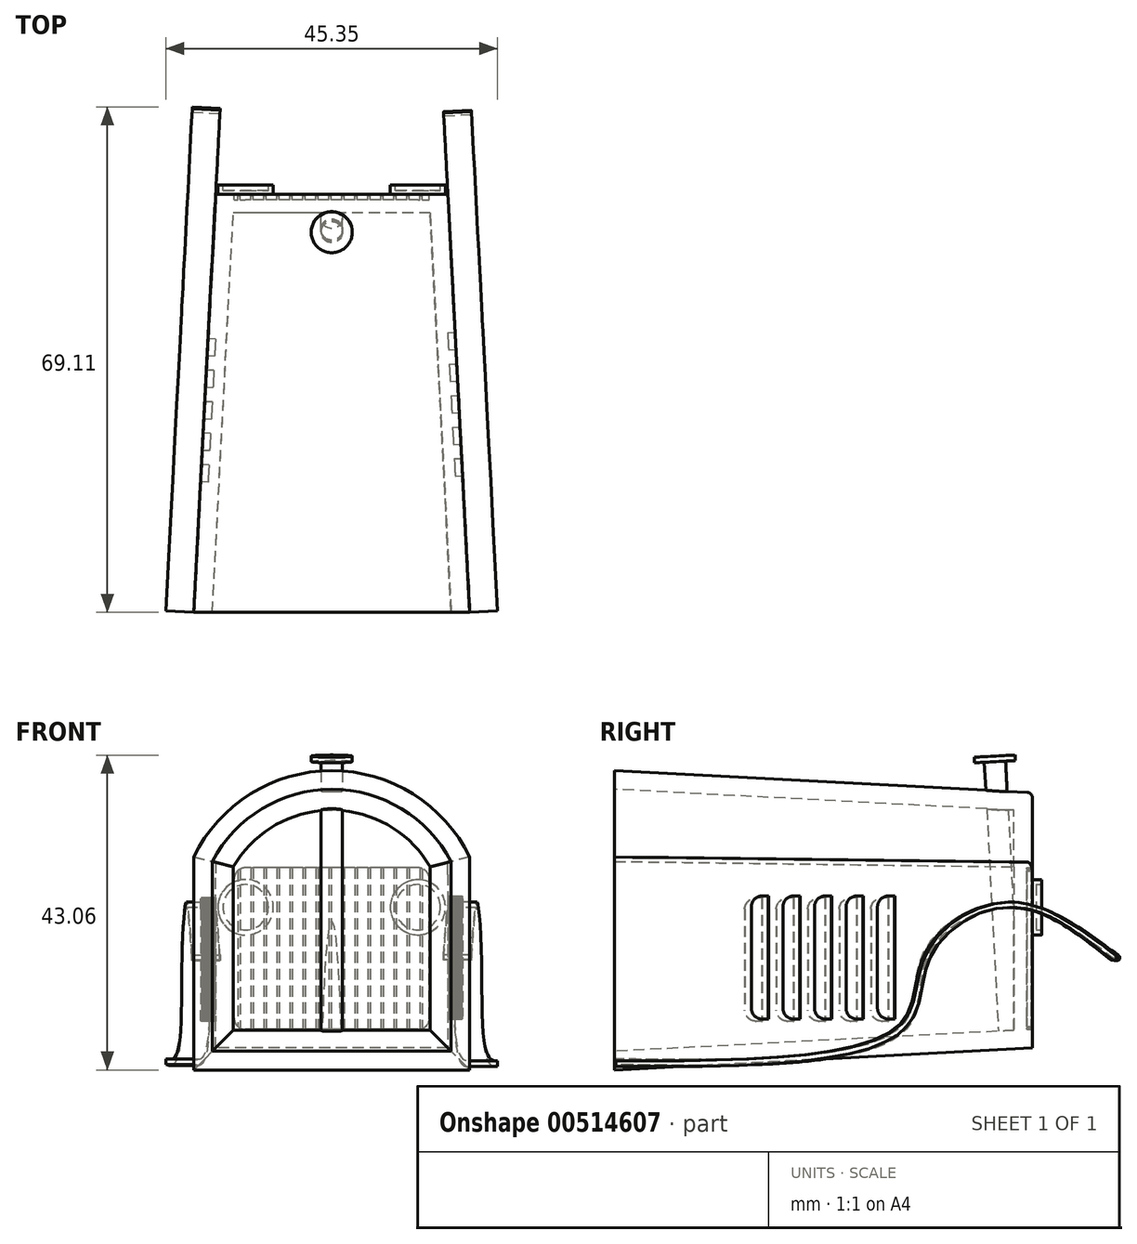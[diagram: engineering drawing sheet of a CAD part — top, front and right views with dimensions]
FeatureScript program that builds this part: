
annotation { "Feature Type Name" : "Feature", "Feature Type Description" : "" }
export const myFeature = defineFeature(function(context is Context, id is Id, definition is map)
    precondition{}
    {
        {
            var Q0;
            Q0=qCreatedBy(makeId("Front.planeOp"),FACE);
            var sketch = newSketch(context, id + "F0", { "sketchPlane" : qUnion([Q0])});
            skLineSegment(sketch, "E0.bottom", {"start": v(15.88, -12.7) * mm, "end": v(-15.88, -12.7) * mm});
            skLineSegment(sketch, "E0.top", {"start": v(15.88, 12.7) * mm, "end": v(-15.88, 12.7) * mm});
            skLineSegment(sketch, "E0.left", {"start": v(15.88, -12.7) * mm, "end": v(15.88, 12.7) * mm});
            skLineSegment(sketch, "E0.right", {"start": v(-15.88, -12.7) * mm, "end": v(-15.88, 12.7) * mm});
            skPoint(sketch, "E0.middle", {"position": v(0, 0) * mm});
            skArc(sketch, "E1", {"start": v(15.88, 12.7) * mm, "mid": v(0, 22.23) * mm, "end": v(-15.88, 12.7) * mm});
            skSolve(sketch);
        }
        {
            var Q0;
            Q0=makeQuery(id+"F0.imprint","IMPRINT",FACE,{"disambiguationData":[TD([[makeQuery(id+"F0.imprint","IMPRINT",EDGE,{"derivedFrom":sQuery(id+"F0.wireOp",EDGE,"E0.bottom")}),-1.0]])]});
            var Q1;
            Q1=makeQuery(id+"F0.imprint","IMPRINT",FACE,{"disambiguationData":[TD([[makeQuery(id+"F0.imprint","IMPRINT",EDGE,{"derivedFrom":sQuery(id+"F0.wireOp",EDGE,"E0.top")}),-1.0]])]});
            extrude(context, id + "F1", {"entities" : qUnion([Q0, Q1]), "depth" : 57.15 * mm, "offsetDistance" : 25.4 * mm, "hasDraft" : true, "draftAngle" : 3 * degree});
        }
        {
            var Q0;
            Q0=makeQuery(id+"F1.opExtrude","CAP_FACE",FACE,{"disambiguationData":[OSD([sQuery(id+"F0.wireOp",EDGE,"E0.bottom"),sQuery(id+"F0.wireOp",EDGE,"E0.left"),sQuery(id+"F0.wireOp",EDGE,"E0.right"),sQuery(id+"F0.wireOp",EDGE,"E1")])],"isStart":false});
            shell(context, id + "F2", {"entities" : qUnion([Q0]), "thickness" : 2.54 * mm});
        }
        {
            var Q0;
            Q0=makeQuery(id+"F1.opExtrude","CAP_FACE",FACE,{"disambiguationData":[OSD([sQuery(id+"F0.wireOp",EDGE,"E0.bottom"),sQuery(id+"F0.wireOp",EDGE,"E0.left"),sQuery(id+"F0.wireOp",EDGE,"E0.right"),sQuery(id+"F0.wireOp",EDGE,"E1")])],"isStart":true});
            var sketch = newSketch(context, id + "F3", { "sketchPlane" : qUnion([Q0])});
            skLineSegment(sketch, "E2.0", {"start": v(-13.33, -8.64) * mm, "end": v(-13.34, 10.41) * mm});
            skLineSegment(sketch, "E2.1", {"start": v(-11.81, -10.16) * mm, "end": v(11.81, -10.16) * mm});
            skLineSegment(sketch, "E2.2", {"start": v(13.33, -8.64) * mm, "end": v(13.33, 10.41) * mm});
            skLineSegment(sketch, "E3", {"start": v(-11.81, 11.94) * mm, "end": v(11.81, 11.94) * mm});
            skPoint(sketch, "E4.visualSharp", {"position": v(-13.33, 11.94) * mm});
            skArc(sketch, "E4.filletArc", {"start": v(-11.81, 11.94) * mm, "mid": v(-12.89, 11.5) * mm, "end": v(-13.33, 10.41) * mm});
            skPoint(sketch, "E5.visualSharp", {"position": v(13.33, 11.94) * mm});
            skArc(sketch, "E5.filletArc", {"start": v(13.33, 10.41) * mm, "mid": v(12.89, 11.5) * mm, "end": v(11.81, 11.94) * mm});
            skPoint(sketch, "E6.visualSharp", {"position": v(13.33, -10.16) * mm});
            skArc(sketch, "E6.filletArc", {"start": v(11.81, -10.16) * mm, "mid": v(12.89, -9.71) * mm, "end": v(13.33, -8.64) * mm});
            skPoint(sketch, "E7.visualSharp", {"position": v(-13.33, -10.16) * mm});
            skArc(sketch, "E7.filletArc", {"start": v(-13.33, -8.64) * mm, "mid": v(-12.89, -9.71) * mm, "end": v(-11.81, -10.16) * mm});
            skSolve(sketch);
        }
        {
            var Q0;
            Q0 = qSketchRegion(id + "F3", true);
            extrude(context, id + "F4", {"entities" : qUnion([Q0]), "operationType" : NewBodyOperationType.REMOVE, "oppositeDirection" : true, "depth" : 0.76 * mm, "offsetDistance" : 25.4 * mm});
        }
        {
            var Q0;
            Q0=makeQuery(id+"F1.opExtrude","SWEPT_FACE",FACE,{"disambiguationData":[OSD([sQuery(id+"F0.wireOp",EDGE,"E0.right")])]});
            var sketch = newSketch(context, id + "F5", { "sketchPlane" : qUnion([Q0])});
            skLineSegment(sketch, "E8.bottom", {"start": v(20.57, 7.81) * mm, "end": v(21.4, 7.81) * mm});
            skLineSegment(sketch, "E8.top", {"start": v(20.57, -9.03) * mm, "end": v(21.4, -9.03) * mm});
            skLineSegment(sketch, "E8.left", {"start": v(20.57, 7.81) * mm, "end": v(20.57, -9.03) * mm});
            skLineSegment(sketch, "E8.right", {"start": v(22.93, 6.3) * mm, "end": v(22.93, -7.5) * mm});
            skPoint(sketch, "E9.visualSharp", {"position": v(22.93, 7.81) * mm});
            skArc(sketch, "E9.filletArc", {"start": v(22.93, 6.3) * mm, "mid": v(22.49, 7.37) * mm, "end": v(21.4, 7.81) * mm});
            skPoint(sketch, "E10.visualSharp", {"position": v(22.93, -9.03) * mm});
            skArc(sketch, "E10.filletArc", {"start": v(21.4, -9.03) * mm, "mid": v(22.49, -8.59) * mm, "end": v(22.93, -7.5) * mm});
            skLineSegment(sketch, "E11.1.0.0", {"start": v(24.9, 7.81) * mm, "end": v(24.9, -9.03) * mm});
            skLineSegment(sketch, "E11.1.0.1", {"start": v(27.25, 6.3) * mm, "end": v(27.25, -7.5) * mm});
            skLineSegment(sketch, "E11.1.0.2", {"start": v(24.9, 7.81) * mm, "end": v(25.73, 7.81) * mm});
            skArc(sketch, "E11.1.0.3", {"start": v(27.25, 6.3) * mm, "mid": v(26.8, 7.37) * mm, "end": v(25.73, 7.81) * mm});
            skLineSegment(sketch, "E11.1.0.4", {"start": v(24.9, -9.03) * mm, "end": v(25.73, -9.03) * mm});
            skArc(sketch, "E11.1.0.5", {"start": v(25.73, -9.03) * mm, "mid": v(26.8, -8.59) * mm, "end": v(27.25, -7.5) * mm});
            skLineSegment(sketch, "E11.2.0.0", {"start": v(29.2, 7.81) * mm, "end": v(29.2, -9.03) * mm});
            skLineSegment(sketch, "E11.2.0.1", {"start": v(31.57, 6.3) * mm, "end": v(31.57, -7.5) * mm});
            skLineSegment(sketch, "E11.2.0.2", {"start": v(29.2, 7.81) * mm, "end": v(30.05, 7.81) * mm});
            skArc(sketch, "E11.2.0.3", {"start": v(31.57, 6.3) * mm, "mid": v(31.12, 7.37) * mm, "end": v(30.05, 7.81) * mm});
            skLineSegment(sketch, "E11.2.0.4", {"start": v(29.2, -9.03) * mm, "end": v(30.05, -9.03) * mm});
            skArc(sketch, "E11.2.0.5", {"start": v(30.05, -9.03) * mm, "mid": v(31.12, -8.59) * mm, "end": v(31.57, -7.5) * mm});
            skLineSegment(sketch, "E11.3.0.0", {"start": v(33.53, 7.81) * mm, "end": v(33.53, -9.03) * mm});
            skLineSegment(sketch, "E11.3.0.1", {"start": v(35.89, 6.3) * mm, "end": v(35.89, -7.5) * mm});
            skLineSegment(sketch, "E11.3.0.2", {"start": v(33.53, 7.81) * mm, "end": v(34.36, 7.81) * mm});
            skArc(sketch, "E11.3.0.3", {"start": v(35.89, 6.3) * mm, "mid": v(35.44, 7.37) * mm, "end": v(34.36, 7.81) * mm});
            skLineSegment(sketch, "E11.3.0.4", {"start": v(33.53, -9.03) * mm, "end": v(34.36, -9.03) * mm});
            skArc(sketch, "E11.3.0.5", {"start": v(34.36, -9.03) * mm, "mid": v(35.44, -8.59) * mm, "end": v(35.89, -7.5) * mm});
            skLineSegment(sketch, "E11.4.0.0", {"start": v(37.85, 7.81) * mm, "end": v(37.85, -9.03) * mm});
            skLineSegment(sketch, "E11.4.0.1", {"start": v(40.2, 6.3) * mm, "end": v(40.2, -7.5) * mm});
            skLineSegment(sketch, "E11.4.0.2", {"start": v(37.85, 7.81) * mm, "end": v(38.68, 7.81) * mm});
            skArc(sketch, "E11.4.0.3", {"start": v(40.2, 6.3) * mm, "mid": v(39.76, 7.37) * mm, "end": v(38.68, 7.81) * mm});
            skLineSegment(sketch, "E11.4.0.4", {"start": v(37.85, -9.03) * mm, "end": v(38.68, -9.03) * mm});
            skArc(sketch, "E11.4.0.5", {"start": v(38.68, -9.03) * mm, "mid": v(39.76, -8.59) * mm, "end": v(40.2, -7.5) * mm});
            skLineSegment(sketch, "E11.direction1", {"start": v(20.57, -9.03) * mm, "end": v(24.9, -9.03) * mm, "construction": true});
            skSolve(sketch);
        }
        {
            var Q0;
            Q0 = qSketchRegion(id + "F5", true);
            extrude(context, id + "F6", {"entities" : qUnion([Q0]), "operationType" : NewBodyOperationType.REMOVE, "oppositeDirection" : true, "depth" : 1.02 * mm, "offsetDistance" : 25.4 * mm});
        }
        {
            var Q0;
            Q0=makeQuery(id+"F1.opExtrude","CAP_EDGE",EDGE,{"disambiguationData":[OSD([sQuery(id+"F0.wireOp",EDGE,"E1")])],"isStart":true});
            fillet(context, id + "F7", {"entities" : qUnion([Q0]), "radius" : 0.76 * mm, "tangentPropagation" : true, "allowEdgeOverflow" : false});
        }
        {
            var Q0;
            Q0=makeQuery(id+"F1.opExtrude","SWEPT_FACE",FACE,{"disambiguationData":[OSD([sQuery(id+"F0.wireOp",EDGE,"E0.left")])]});
            var sketch = newSketch(context, id + "F8", { "sketchPlane" : qUnion([Q0])});
            skPoint(sketch, "E12.visualSharp", {"position": v(-36.83, 8.1) * mm});
            skPoint(sketch, "E13.visualSharp", {"position": v(-36.83, -8.75) * mm});
            skLineSegment(sketch, "E14.MirrorCS", {"start": v(-24.02, -8.75) * mm, "end": v(-24.86, -8.75) * mm});
            skLineSegment(sketch, "E15.MirrorCS", {"start": v(-28.34, 8.1) * mm, "end": v(-29.17, 8.1) * mm});
            skLineSegment(sketch, "E16.MirrorCS", {"start": v(-19.7, -8.75) * mm, "end": v(-20.54, -8.75) * mm});
            skLineSegment(sketch, "E17.MirrorCS", {"start": v(-24.02, 8.1) * mm, "end": v(-24.86, 8.1) * mm});
            skLineSegment(sketch, "E18.MirrorCS", {"start": v(-32.65, -8.75) * mm, "end": v(-33.5, -8.75) * mm});
            skLineSegment(sketch, "E19.MirrorCS", {"start": v(-19.7, 8.1) * mm, "end": v(-20.54, 8.1) * mm});
            skLineSegment(sketch, "E20.MirrorCS", {"start": v(-36.97, 8.1) * mm, "end": v(-37.8, 8.1) * mm});
            skLineSegment(sketch, "E21.MirrorCS", {"start": v(-28.34, -8.75) * mm, "end": v(-29.17, -8.75) * mm});
            skLineSegment(sketch, "E22.MirrorCS", {"start": v(-32.65, 8.1) * mm, "end": v(-33.5, 8.1) * mm});
            skLineSegment(sketch, "E23.MirrorCS", {"start": v(-36.97, -8.75) * mm, "end": v(-37.8, -8.75) * mm});
            skArc(sketch, "E24.MirrorCS", {"start": v(-22.06, 6.57) * mm, "mid": v(-21.61, 7.65) * mm, "end": v(-20.54, 8.1) * mm});
            skArc(sketch, "E25.MirrorCS", {"start": v(-20.54, -8.75) * mm, "mid": v(-21.61, -8.3) * mm, "end": v(-22.06, -7.23) * mm});
            skArc(sketch, "E26.MirrorCS", {"start": v(-30.7, 6.57) * mm, "mid": v(-30.25, 7.65) * mm, "end": v(-29.17, 8.1) * mm});
            skLineSegment(sketch, "E27.MirrorCS", {"start": v(-19.7, 8.1) * mm, "end": v(-19.7, -8.75) * mm});
            skLineSegment(sketch, "E28.MirrorCS", {"start": v(-36.97, 8.1) * mm, "end": v(-36.97, -8.75) * mm});
            skLineSegment(sketch, "E29.MirrorCS", {"start": v(-22.06, 6.57) * mm, "end": v(-22.06, -7.23) * mm});
            skArc(sketch, "E30.MirrorCS", {"start": v(-24.86, -8.75) * mm, "mid": v(-25.93, -8.3) * mm, "end": v(-26.38, -7.23) * mm});
            skLineSegment(sketch, "E31.MirrorCS", {"start": v(-32.65, 8.1) * mm, "end": v(-32.65, -8.75) * mm});
            skLineSegment(sketch, "E32.MirrorCS", {"start": v(-30.7, 6.57) * mm, "end": v(-30.7, -7.23) * mm});
            skLineSegment(sketch, "E33.MirrorCS", {"start": v(-39.33, 6.57) * mm, "end": v(-39.33, -7.23) * mm});
            skLineSegment(sketch, "E34.MirrorCS", {"start": v(-24.02, 8.1) * mm, "end": v(-24.02, -8.75) * mm});
            skLineSegment(sketch, "E35.MirrorCS", {"start": v(-26.38, 6.57) * mm, "end": v(-26.38, -7.23) * mm});
            skArc(sketch, "E36.MirrorCS", {"start": v(-26.38, 6.57) * mm, "mid": v(-25.93, 7.65) * mm, "end": v(-24.86, 8.1) * mm});
            skLineSegment(sketch, "E37.MirrorCS", {"start": v(-28.34, 8.1) * mm, "end": v(-28.34, -8.75) * mm});
            skLineSegment(sketch, "E38.MirrorCS", {"start": v(-35.02, 6.57) * mm, "end": v(-35.02, -7.23) * mm});
            skPoint(sketch, "E39.MirrorP", {"position": v(-22.06, 8.1) * mm});
            skArc(sketch, "E40.MirrorCS", {"start": v(-39.33, 6.57) * mm, "mid": v(-38.89, 7.65) * mm, "end": v(-37.8, 8.1) * mm});
            skArc(sketch, "E41.MirrorCS", {"start": v(-37.8, -8.75) * mm, "mid": v(-38.89, -8.3) * mm, "end": v(-39.33, -7.23) * mm});
            skArc(sketch, "E42.MirrorCS", {"start": v(-33.5, -8.75) * mm, "mid": v(-34.57, -8.3) * mm, "end": v(-35.02, -7.23) * mm});
            skArc(sketch, "E43.MirrorCS", {"start": v(-29.17, -8.75) * mm, "mid": v(-30.25, -8.3) * mm, "end": v(-30.7, -7.23) * mm});
            skArc(sketch, "E44.MirrorCS", {"start": v(-35.02, 6.57) * mm, "mid": v(-34.57, 7.65) * mm, "end": v(-33.5, 8.1) * mm});
            skSolve(sketch);
        }
        {
            var Q0;
            Q0 = qSketchRegion(id + "F8", true);
            extrude(context, id + "F9", {"entities" : qUnion([Q0]), "operationType" : NewBodyOperationType.REMOVE, "oppositeDirection" : true, "depth" : 1.02 * mm, "offsetDistance" : 25.4 * mm});
        }
        {
            var Q0;
            Q0=makeQuery(id+"F1.opExtrude","SWEPT_FACE",FACE,{"disambiguationData":[OSD([sQuery(id+"F0.wireOp",EDGE,"E0.right")])]});
            var sketch = newSketch(context, id + "F10", { "sketchPlane" : qUnion([Q0])});
            skPoint(sketch, "E45.4.internal.snap0", {"position": v(29.45, -14.2) * mm});
            skFitSpline(sketch, "E45", {"points": [v(-10.7, 0) * mm, v(4.58, 7.25) * mm, v(15.95, 0) * mm, v(18.97, -9.69) * mm, v(58.06, -14.2) * mm], "startDerivative": vector(62.95, 46.66) * mm, "endDerivative": vector(141.94, 1.74) * mm});
            skFitSpline(sketch, "E46.0", {"points": [v(-10.24, -0.61) * mm, v(-8.93, 0.36) * mm, v(-6.32, 2.3) * mm, v(-2.43, 4.74) * mm, v(0.78, 6.07) * mm, v(3.34, 6.52) * mm, v(5.26, 6.5) * mm, v(7.22, 6.13) * mm, v(9.13, 5.43) * mm, v(10.92, 4.46) * mm, v(12.54, 3.26) * mm, v(13.9, 1.88) * mm, v(14.8, 0.63) * mm, v(15.3, -0.4) * mm, v(15.7, -1.45) * mm, v(16.03, -2.84) * mm, v(16.28, -4.58) * mm, v(16.54, -6.33) * mm, v(16.93, -7.78) * mm, v(17.43, -8.89) * mm, v(17.94, -9.69) * mm, v(18.6, -10.43) * mm, v(19.38, -11.09) * mm, v(20.3, -11.67) * mm, v(21.67, -12.36) * mm, v(23.65, -13.07) * mm, v(26.44, -13.74) * mm, v(29.59, -14.24) * mm, v(34.21, -14.72) * mm, v(40.68, -15.02) * mm, v(49.2, -15.07) * mm, v(55.11, -15) * mm, v(58.07, -14.96) * mm]});
            skArc(sketch, "E47", {"start": v(-10.7, 0) * mm, "mid": v(-10.85, -0.6) * mm, "end": v(-10.24, -0.61) * mm});
            skLineSegment(sketch, "E48", {"start": v(58.06, -14.2) * mm, "end": v(58.07, -14.96) * mm});
            skSolve(sketch);
        }
        {
            var Q0;
            Q0=makeQuery(id+"F1.opExtrude","SWEPT_FACE",FACE,{"disambiguationData":[OSD([sQuery(id+"F0.wireOp",EDGE,"E0.left")])]});
            var sketch = newSketch(context, id + "F11", { "sketchPlane" : qUnion([Q0])});
            skPoint(sketch, "E49.4.internal.snap0", {"position": v(-29.45, -14.2) * mm});
            skFitSpline(sketch, "E50", {"points": [v(10.33, 0) * mm, v(-4.5, 7.25) * mm, v(-15.7, 0) * mm, v(-19.07, -9.51) * mm, v(-58.06, -14.48) * mm], "startDerivative": vector(-61.62, 47.02) * mm, "endDerivative": vector(-140.12, -0.34) * mm});
            skFitSpline(sketch, "E51.0", {"points": [v(9.86, -0.6) * mm, v(8.58, 0.37) * mm, v(6.03, 2.32) * mm, v(2.22, 4.78) * mm, v(-0.91, 6.1) * mm, v(-3.1, 6.47) * mm, v(-4.34, 6.51) * mm, v(-5.59, 6.43) * mm, v(-7.17, 6.1) * mm, v(-9.03, 5.37) * mm, v(-10.78, 4.38) * mm, v(-12.36, 3.16) * mm, v(-13.7, 1.78) * mm, v(-14.58, 0.52) * mm, v(-15.1, -0.5) * mm, v(-15.52, -1.55) * mm, v(-15.87, -2.92) * mm, v(-16.18, -4.63) * mm, v(-16.53, -6.34) * mm, v(-16.99, -7.75) * mm, v(-17.55, -8.84) * mm, v(-18.1, -9.6) * mm, v(-18.79, -10.32) * mm, v(-19.6, -10.96) * mm, v(-20.54, -11.54) * mm, v(-21.93, -12.22) * mm, v(-23.94, -12.93) * mm, v(-26.73, -13.61) * mm, v(-29.87, -14.14) * mm, v(-34.47, -14.67) * mm, v(-40.88, -15.05) * mm, v(-49.3, -15.22) * mm, v(-55.14, -15.23) * mm, v(-58.06, -15.24) * mm]});
            skArc(sketch, "E52", {"start": v(9.86, -0.6) * mm, "mid": v(10.41, -0.54) * mm, "end": v(10.33, 0) * mm});
            skLineSegment(sketch, "E53", {"start": v(-58.06, -14.48) * mm, "end": v(-58.06, -15.24) * mm});
            skSolve(sketch);
        }
        {
            var Q0;
            Q0=makeQuery(id+"F1.opExtrude","SWEPT_FACE",FACE,{"disambiguationData":[OSD([sQuery(id+"F0.wireOp",EDGE,"E0.bottom")])]});
            var sketch = newSketch(context, id + "F12", { "sketchPlane" : qUnion([Q0])});
            skCircle(sketch, "E54", {"center": v(0, 3.75) * mm, "radius": 1.46 * mm});
            skSolve(sketch);
        }
        {
            var Q0;
            Q0 = qSketchRegion(id + "F12", true);
            extrude(context, id + "F13", {"entities" : qUnion([Q0]), "operationType" : NewBodyOperationType.ADD, "depth" : -39.37 * mm, "offsetDistance" : 25.4 * mm});
        }
        {
            var Q0;
            Q0=makeQuery(id+"F13.opExtrude","CAP_FACE",FACE,{"disambiguationData":[OSD([sQuery(id+"F12.wireOp",EDGE,"E54")])],"isStart":false});
            var sketch = newSketch(context, id + "F14", { "sketchPlane" : qUnion([Q0])});
            skCircle(sketch, "E55", {"center": v(0, -3.75) * mm, "radius": 2.8 * mm});
            skSolve(sketch);
        }
        {
            var Q0;
            Q0 = qSketchRegion(id + "F14", true);
            extrude(context, id + "F15", {"entities" : qUnion([Q0]), "operationType" : NewBodyOperationType.ADD, "depth" : 0.76 * mm, "offsetDistance" : 25.4 * mm});
        }
        {
            var Q0;
            Q0 = qSketchRegion(id + "F11", true);
            var Q1;
            Q1=sQuery(id+"F11.wireOp",EDGE,"E50");
            extrude(context, id + "F16", {"entities" : qUnion([Q0]), "operationType" : NewBodyOperationType.ADD, "surfaceEntities" : qUnion([Q1]), "depth" : 3.8 * mm, "offsetDistance" : 25.4 * mm});
        }
        {
            var Q0;
            Q0 = qSketchRegion(id + "F10", true);
            var Q1;
            Q1 = qConstructionFilter(qBodyType(qCreatedBy(id + "F10" ,EDGE), BodyType.WIRE), ConstructionObject.NO);
            extrude(context, id + "F17", {"entities" : qUnion([Q0]), "operationType" : NewBodyOperationType.ADD, "surfaceEntities" : qUnion([Q1]), "depth" : 3.8 * mm, "offsetDistance" : 25.4 * mm});
        }
        {
            var Q0;
            Q0=makeQuery(id+"F1.opExtrude","CAP_FACE",FACE,{"disambiguationData":[OSD([sQuery(id+"F0.wireOp",EDGE,"E0.bottom"),sQuery(id+"F0.wireOp",EDGE,"E0.left"),sQuery(id+"F0.wireOp",EDGE,"E0.right"),sQuery(id+"F0.wireOp",EDGE,"E1")])],"isStart":true});
            var sketch = newSketch(context, id + "F18", { "sketchPlane" : qUnion([Q0])});
            skCircle(sketch, "E56", {"center": v(11.78, 6.54) * mm, "radius": 3.79 * mm});
            skCircle(sketch, "E57", {"center": v(-11.78, 6.54) * mm, "radius": 3.77 * mm});
            skSolve(sketch);
        }
        {
            var Q0;
            Q0 = qSketchRegion(id + "F18", true);
            extrude(context, id + "F19", {"entities" : qUnion([Q0]), "operationType" : NewBodyOperationType.ADD, "depth" : 1.27 * mm, "offsetDistance" : 25.4 * mm});
        }
        {
            var Q0;
            Q0=makeQuery(id+"F19.opExtrude","CAP_FACE",FACE,{"disambiguationData":[OSD([sQuery(id+"F18.wireOp",EDGE,"E56")])],"isStart":false});
            var sketch = newSketch(context, id + "F20", { "sketchPlane" : qUnion([Q0])});
            skCircle(sketch, "E58", {"center": v(11.78, 6.54) * mm, "radius": 3.1 * mm});
            skSolve(sketch);
        }
        {
            var Q0;
            Q0=makeQuery(id+"F19.opExtrude","CAP_FACE",FACE,{"disambiguationData":[OSD([sQuery(id+"F18.wireOp",EDGE,"E57")])],"isStart":false});
            var sketch = newSketch(context, id + "F21", { "sketchPlane" : qUnion([Q0])});
            skCircle(sketch, "E59", {"center": v(-11.78, 6.54) * mm, "radius": 3.1 * mm});
            skSolve(sketch);
        }
        {
            var Q0;
            Q0=makeQuery(id+"F21.imprint","IMPRINT",FACE,{"disambiguationData":[TD([[makeQuery(id+"F21.imprint","IMPRINT",EDGE,{"derivedFrom":sQuery(id+"F21.wireOp",EDGE,"E59")}),1.0]])]});
            var Q1;
            Q1=makeQuery(id+"F20.imprint","IMPRINT",FACE,{"disambiguationData":[TD([[makeQuery(id+"F20.imprint","IMPRINT",EDGE,{"derivedFrom":sQuery(id+"F20.wireOp",EDGE,"E58")}),1.0]])]});
            var Q2;
            Q2=sQuery(id+"F21.wireOp",EDGE,"E59");
            var Q3;
            Q3=sQuery(id+"F20.wireOp",EDGE,"E58");
            extrude(context, id + "F22", {"entities" : qUnion([Q0, Q1]), "operationType" : NewBodyOperationType.REMOVE, "surfaceEntities" : qUnion([Q2, Q3]), "oppositeDirection" : true, "depth" : 0.76 * mm, "offsetDistance" : 25.4 * mm});
        }
        {
            var Q0;
            Q0=makeQuery(id+"F4.boolean.opBoolean","COPY",FACE,{"derivedFrom":makeQuery(id+"F4.opExtrude","CAP_FACE",FACE,{"disambiguationData":[OSD([sQuery(id+"F3.wireOp",EDGE,"E2.0"),sQuery(id+"F3.wireOp",EDGE,"E2.1"),sQuery(id+"F3.wireOp",EDGE,"E2.2"),sQuery(id+"F3.wireOp",EDGE,"E3"),sQuery(id+"F3.wireOp",EDGE,"E4.filletArc"),sQuery(id+"F3.wireOp",EDGE,"E5.filletArc"),sQuery(id+"F3.wireOp",EDGE,"E6.filletArc"),sQuery(id+"F3.wireOp",EDGE,"E7.filletArc")])],"isStart":false})});
            var sketch = newSketch(context, id + "F23", { "sketchPlane" : qUnion([Q0])});
            skLineSegment(sketch, "E60.bottom", {"start": v(-12.05, 12.25) * mm, "end": v(-12.4, 12.25) * mm});
            skLineSegment(sketch, "E60.top", {"start": v(-12.05, -10.76) * mm, "end": v(-12.4, -10.76) * mm});
            skLineSegment(sketch, "E60.left", {"start": v(-12.05, 12.25) * mm, "end": v(-12.05, -10.76) * mm});
            skLineSegment(sketch, "E60.right", {"start": v(-12.4, 12.25) * mm, "end": v(-12.4, -10.76) * mm});
            skLineSegment(sketch, "E61.1.0.0", {"start": v(-10.61, 12.25) * mm, "end": v(-10.61, -10.76) * mm});
            skLineSegment(sketch, "E61.1.0.1", {"start": v(-10.27, 12.25) * mm, "end": v(-10.27, -10.76) * mm});
            skLineSegment(sketch, "E61.1.0.2", {"start": v(-10.27, -10.76) * mm, "end": v(-10.61, -10.76) * mm});
            skLineSegment(sketch, "E61.1.0.3", {"start": v(-10.27, 12.25) * mm, "end": v(-10.61, 12.25) * mm});
            skLineSegment(sketch, "E61.2.0.0", {"start": v(-8.84, 12.25) * mm, "end": v(-8.84, -10.76) * mm});
            skLineSegment(sketch, "E61.2.0.1", {"start": v(-8.49, 12.25) * mm, "end": v(-8.49, -10.76) * mm});
            skLineSegment(sketch, "E61.2.0.2", {"start": v(-8.49, -10.76) * mm, "end": v(-8.84, -10.76) * mm});
            skLineSegment(sketch, "E61.2.0.3", {"start": v(-8.49, 12.25) * mm, "end": v(-8.84, 12.25) * mm});
            skLineSegment(sketch, "E61.3.0.0", {"start": v(-7.06, 12.25) * mm, "end": v(-7.06, -10.76) * mm});
            skLineSegment(sketch, "E61.3.0.1", {"start": v(-6.71, 12.25) * mm, "end": v(-6.71, -10.76) * mm});
            skLineSegment(sketch, "E61.3.0.2", {"start": v(-6.71, -10.76) * mm, "end": v(-7.06, -10.76) * mm});
            skLineSegment(sketch, "E61.3.0.3", {"start": v(-6.71, 12.25) * mm, "end": v(-7.06, 12.25) * mm});
            skLineSegment(sketch, "E61.4.0.0", {"start": v(-5.28, 12.25) * mm, "end": v(-5.28, -10.76) * mm});
            skLineSegment(sketch, "E61.4.0.1", {"start": v(-4.93, 12.25) * mm, "end": v(-4.93, -10.76) * mm});
            skLineSegment(sketch, "E61.4.0.2", {"start": v(-4.93, -10.76) * mm, "end": v(-5.28, -10.76) * mm});
            skLineSegment(sketch, "E61.4.0.3", {"start": v(-4.93, 12.25) * mm, "end": v(-5.28, 12.25) * mm});
            skLineSegment(sketch, "E61.5.0.0", {"start": v(-3.5, 12.25) * mm, "end": v(-3.5, -10.76) * mm});
            skLineSegment(sketch, "E61.5.0.1", {"start": v(-3.16, 12.25) * mm, "end": v(-3.16, -10.76) * mm});
            skLineSegment(sketch, "E61.5.0.2", {"start": v(-3.16, -10.76) * mm, "end": v(-3.5, -10.76) * mm});
            skLineSegment(sketch, "E61.5.0.3", {"start": v(-3.16, 12.25) * mm, "end": v(-3.5, 12.25) * mm});
            skLineSegment(sketch, "E61.6.0.0", {"start": v(-1.72, 12.25) * mm, "end": v(-1.72, -10.76) * mm});
            skLineSegment(sketch, "E61.6.0.1", {"start": v(-1.38, 12.25) * mm, "end": v(-1.38, -10.76) * mm});
            skLineSegment(sketch, "E61.6.0.2", {"start": v(-1.38, -10.76) * mm, "end": v(-1.72, -10.76) * mm});
            skLineSegment(sketch, "E61.6.0.3", {"start": v(-1.38, 12.25) * mm, "end": v(-1.72, 12.25) * mm});
            skLineSegment(sketch, "E61.7.0.0", {"start": v(0.05, 12.25) * mm, "end": v(0.05, -10.76) * mm});
            skLineSegment(sketch, "E61.7.0.1", {"start": v(0.4, 12.25) * mm, "end": v(0.4, -10.76) * mm});
            skLineSegment(sketch, "E61.7.0.2", {"start": v(0.4, -10.76) * mm, "end": v(0.05, -10.76) * mm});
            skLineSegment(sketch, "E61.7.0.3", {"start": v(0.4, 12.25) * mm, "end": v(0.05, 12.25) * mm});
            skLineSegment(sketch, "E61.8.0.0", {"start": v(1.83, 12.25) * mm, "end": v(1.83, -10.76) * mm});
            skLineSegment(sketch, "E61.8.0.1", {"start": v(2.18, 12.25) * mm, "end": v(2.18, -10.76) * mm});
            skLineSegment(sketch, "E61.8.0.2", {"start": v(2.18, -10.76) * mm, "end": v(1.83, -10.76) * mm});
            skLineSegment(sketch, "E61.8.0.3", {"start": v(2.18, 12.25) * mm, "end": v(1.83, 12.25) * mm});
            skLineSegment(sketch, "E61.9.0.0", {"start": v(3.6, 12.25) * mm, "end": v(3.6, -10.76) * mm});
            skLineSegment(sketch, "E61.9.0.1", {"start": v(3.96, 12.25) * mm, "end": v(3.96, -10.76) * mm});
            skLineSegment(sketch, "E61.9.0.2", {"start": v(3.96, -10.76) * mm, "end": v(3.6, -10.76) * mm});
            skLineSegment(sketch, "E61.9.0.3", {"start": v(3.96, 12.25) * mm, "end": v(3.6, 12.25) * mm});
            skLineSegment(sketch, "E61.10.0.0", {"start": v(5.39, 12.25) * mm, "end": v(5.39, -10.76) * mm});
            skLineSegment(sketch, "E61.10.0.1", {"start": v(5.73, 12.25) * mm, "end": v(5.73, -10.76) * mm});
            skLineSegment(sketch, "E61.10.0.2", {"start": v(5.73, -10.76) * mm, "end": v(5.39, -10.76) * mm});
            skLineSegment(sketch, "E61.10.0.3", {"start": v(5.73, 12.25) * mm, "end": v(5.39, 12.25) * mm});
            skLineSegment(sketch, "E61.11.0.0", {"start": v(7.17, 12.25) * mm, "end": v(7.17, -10.76) * mm});
            skLineSegment(sketch, "E61.11.0.1", {"start": v(7.51, 12.25) * mm, "end": v(7.51, -10.76) * mm});
            skLineSegment(sketch, "E61.11.0.2", {"start": v(7.51, -10.76) * mm, "end": v(7.17, -10.76) * mm});
            skLineSegment(sketch, "E61.11.0.3", {"start": v(7.51, 12.25) * mm, "end": v(7.17, 12.25) * mm});
            skLineSegment(sketch, "E61.12.0.0", {"start": v(8.94, 12.25) * mm, "end": v(8.94, -10.76) * mm});
            skLineSegment(sketch, "E61.12.0.1", {"start": v(9.3, 12.25) * mm, "end": v(9.3, -10.76) * mm});
            skLineSegment(sketch, "E61.12.0.2", {"start": v(9.3, -10.76) * mm, "end": v(8.94, -10.76) * mm});
            skLineSegment(sketch, "E61.12.0.3", {"start": v(9.3, 12.25) * mm, "end": v(8.94, 12.25) * mm});
            skLineSegment(sketch, "E61.13.0.0", {"start": v(10.72, 12.25) * mm, "end": v(10.72, -10.76) * mm});
            skLineSegment(sketch, "E61.13.0.1", {"start": v(11.07, 12.25) * mm, "end": v(11.07, -10.76) * mm});
            skLineSegment(sketch, "E61.13.0.2", {"start": v(11.07, -10.76) * mm, "end": v(10.72, -10.76) * mm});
            skLineSegment(sketch, "E61.13.0.3", {"start": v(11.07, 12.25) * mm, "end": v(10.72, 12.25) * mm});
            skLineSegment(sketch, "E61.14.0.0", {"start": v(12.5, 12.25) * mm, "end": v(12.5, -10.76) * mm});
            skLineSegment(sketch, "E61.14.0.1", {"start": v(12.85, 12.25) * mm, "end": v(12.85, -10.76) * mm});
            skLineSegment(sketch, "E61.14.0.2", {"start": v(12.85, -10.76) * mm, "end": v(12.5, -10.76) * mm});
            skLineSegment(sketch, "E61.14.0.3", {"start": v(12.85, 12.25) * mm, "end": v(12.5, 12.25) * mm});
            skLineSegment(sketch, "E61.direction1", {"start": v(-12.4, -10.76) * mm, "end": v(-10.61, -10.76) * mm, "construction": true});
            skSolve(sketch);
        }
        {
            var Q0;
            Q0 = qSketchRegion(id + "F23", true);
            extrude(context, id + "F24", {"entities" : qUnion([Q0]), "operationType" : NewBodyOperationType.ADD, "depth" : 0.58 * mm, "offsetDistance" : 25.4 * mm});
        }
    });
